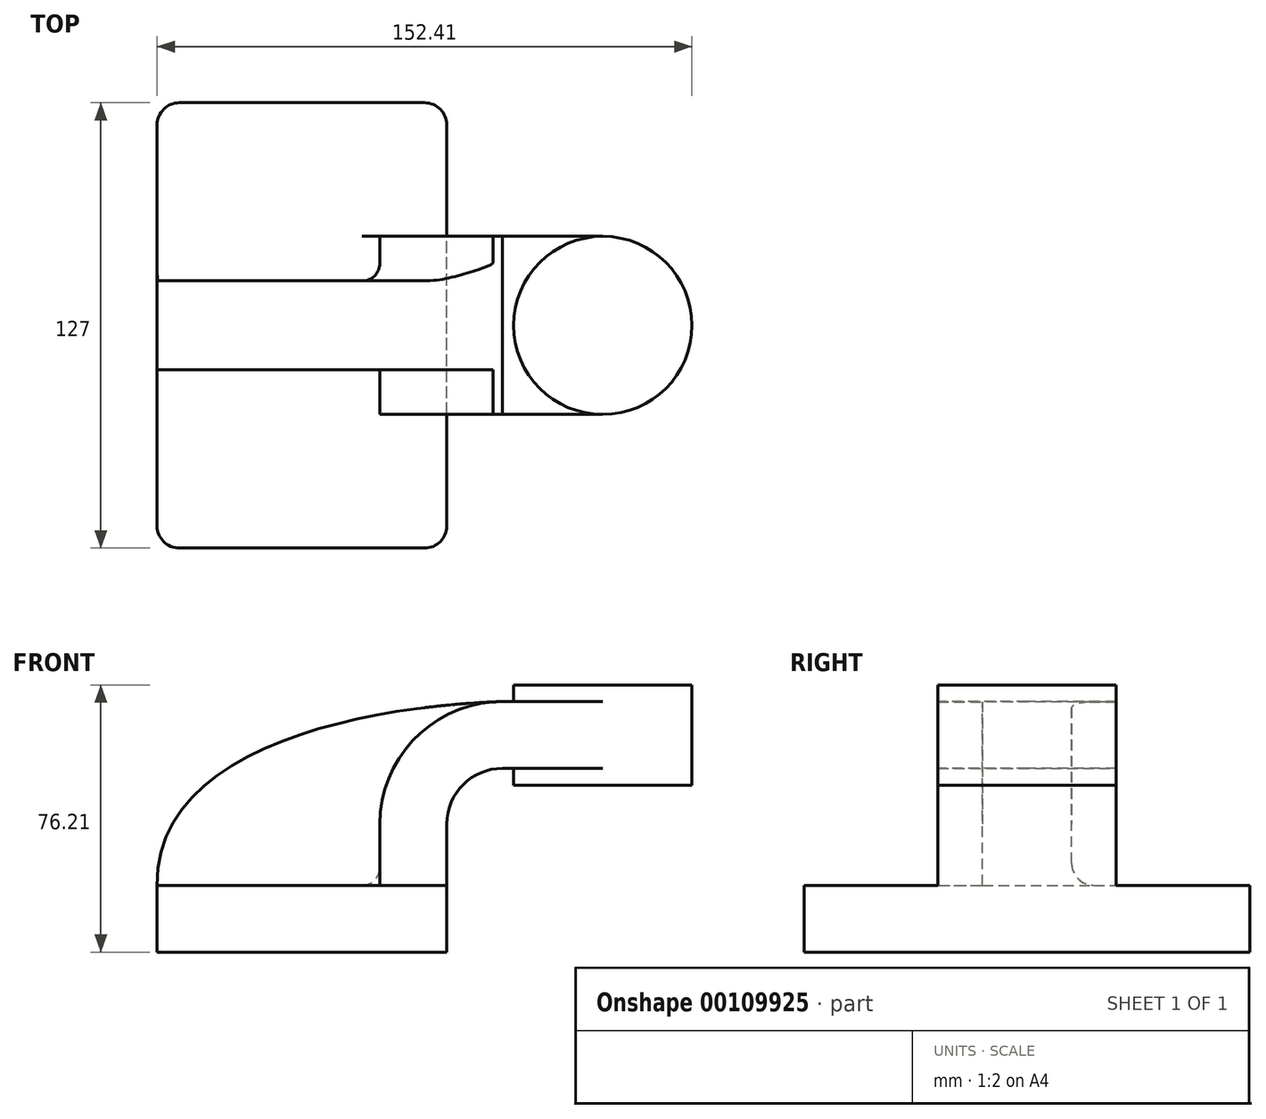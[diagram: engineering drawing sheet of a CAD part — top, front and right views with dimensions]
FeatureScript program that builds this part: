
annotation { "Feature Type Name" : "Feature", "Feature Type Description" : "" }
export const myFeature = defineFeature(function(context is Context, id is Id, definition is map)
    precondition{}
    {
        {
            var Q0;
            Q0=qCreatedBy(makeId("Front.planeOp"),FACE);
            var sketch = newSketch(context, id + "F0", { "sketchPlane" : qUnion([Q0])});
            skLineSegment(sketch, "E0.bottom", {"start": v(-41.27, -9.53) * mm, "end": v(41.28, -9.52) * mm});
            skLineSegment(sketch, "E0.top", {"start": v(-41.28, 9.52) * mm, "end": v(41.27, 9.53) * mm});
            skLineSegment(sketch, "E0.left", {"start": v(-41.27, -9.53) * mm, "end": v(-41.28, 9.52) * mm});
            skLineSegment(sketch, "E0.right", {"start": v(41.28, -9.52) * mm, "end": v(41.27, 9.53) * mm});
            skPoint(sketch, "E0.middle", {"position": v(0, 0) * mm});
            skLineSegment(sketch, "E1.bottom", {"start": v(111.13, 38.1) * mm, "end": v(60.33, 38.1) * mm});
            skLineSegment(sketch, "E1.top", {"start": v(111.13, 66.68) * mm, "end": v(60.33, 66.67) * mm});
            skLineSegment(sketch, "E1.left", {"start": v(111.13, 38.1) * mm, "end": v(111.13, 66.67) * mm});
            skLineSegment(sketch, "E1.right", {"start": v(60.33, 38.1) * mm, "end": v(60.33, 66.67) * mm});
            skPoint(sketch, "E1.middle", {"position": v(85.73, 52.39) * mm});
            skLineSegment(sketch, "E2", {"start": v(41.27, 9.53) * mm, "end": v(41.27, 27) * mm});
            skArc(sketch, "E3", {"start": v(41.28, 27) * mm, "mid": v(45.92, 38.23) * mm, "end": v(57.15, 42.88) * mm});
            skLineSegment(sketch, "E4", {"start": v(57.15, 42.88) * mm, "end": v(85.73, 42.88) * mm});
            skLineSegment(sketch, "E5.0", {"start": v(57.15, 61.93) * mm, "end": v(85.73, 61.93) * mm});
            skArc(sketch, "E5.1", {"start": v(22.23, 27) * mm, "mid": v(32.45, 51.7) * mm, "end": v(57.15, 61.93) * mm});
            skLineSegment(sketch, "E5.2", {"start": v(22.22, 9.53) * mm, "end": v(22.22, 27) * mm});
            skLineSegment(sketch, "E6", {"start": v(85.73, 38.1) * mm, "end": v(85.73, 66.67) * mm});
            skFitSpline(sketch, "E7", {"points": [v(-41.28, 9.52) * mm, v(57.15, 61.93) * mm], "startDerivative": vector(-1.57, 118.9) * mm, "endDerivative": vector(117.7, 4) * mm});
            skSolve(sketch);
        }
        {
            var Q0;
            Q0=makeQuery(id+"F0.imprint","IMPRINT",FACE,{"disambiguationData":[TD([[makeQuery(id+"F0.imprint","IMPRINT",EDGE,{"derivedFrom":sQuery(id+"F0.wireOp",EDGE,"E0.bottom")}),1.0]])]});
            extrude(context, id + "F1", {"entities" : qUnion([Q0]), "endBound" : BoundingType.SYMMETRIC, "depth" : 127 * mm});
        }
        {
            var Q0;
            {var subQ1=sQuery(id+"F0.wireOp",EDGE,"E2");Q0=makeQuery(id+"F0.imprint","IMPRINT",FACE,{"disambiguationData":[TD([[makeQuery(id+"F0.imprint","IMPRINT",EDGE,{"derivedFrom":subQ1}),1.0]])]});}
            extrude(context, id + "F2", {"entities" : qUnion([Q0]), "operationType" : NewBodyOperationType.ADD, "endBound" : BoundingType.SYMMETRIC, "depth" : 50.8 * mm});
        }
        {
            var Q0;
            {var subQ0=sQuery(id+"F0.wireOp",EDGE,"E4");var subQ1=sQuery(id+"F0.wireOp",EDGE,"E1.right");var subQ2=makeQuery(id+"F0.imprint","INTERSECT",VERTEX,{"derivedFrom":[subQ1,subQ0]});Q0=makeQuery(id+"F0.imprint","IMPRINT",FACE,{"disambiguationData":[TD([[makeQuery(id+"F0.imprint","IMPRINT",EDGE,{"disambiguationData":[TD([[subQ2,-1.0]])],"derivedFrom":subQ1}),-1.0]])]});}
            extrude(context, id + "F3", {"entities" : qUnion([Q0]), "operationType" : NewBodyOperationType.ADD, "endBound" : BoundingType.SYMMETRIC, "depth" : 50.8 * mm});
        }
        {
            var Q0;
            {var subQ3=sQuery(id+"F0.wireOp",EDGE,"E5.2");Q0=makeQuery(id+"F0.imprint","IMPRINT",FACE,{"disambiguationData":[TD([[makeQuery(id+"F0.imprint","IMPRINT",EDGE,{"derivedFrom":subQ3}),1.0]])]});}
            extrude(context, id + "F4", {"entities" : qUnion([Q0]), "operationType" : NewBodyOperationType.ADD, "endBound" : BoundingType.SYMMETRIC, "depth" : 25.4 * mm});
        }
        {
            var Q0;
            {var subQ0=sQuery(id+"F0.wireOp",EDGE,"E1.left");Q0=makeQuery(id+"F0.imprint","IMPRINT",FACE,{"disambiguationData":[TD([[makeQuery(id+"F0.imprint","IMPRINT",EDGE,{"derivedFrom":subQ0}),1.0]])]});}
            var Q1;
            Q1=sQuery(id+"F0.wireOp",EDGE,"E6");
            revolve(context, id + "F5", {"operationType" : NewBodyOperationType.ADD, "entities" : qUnion([Q0]), "axis" : qUnion([Q1]), "revolveType" : RevolveType.FULL});
        }
        {
            var Q0;
            Q0=makeQuery(id+"F1.opExtrude","CAP_EDGE",EDGE,{"disambiguationData":[OSD([sQuery(id+"F0.wireOp",EDGE,"E0.right")])],"isStart":false});
            var Q1;
            Q1=makeQuery(id+"F1.opExtrude","CAP_EDGE",EDGE,{"disambiguationData":[OSD([sQuery(id+"F0.wireOp",EDGE,"E0.left")])],"isStart":false});
            var Q2;
            Q2=makeQuery(id+"F1.opExtrude","CAP_EDGE",EDGE,{"disambiguationData":[OSD([sQuery(id+"F0.wireOp",EDGE,"E0.right")])],"isStart":true});
            var Q3;
            Q3=makeQuery(id+"F1.opExtrude","CAP_EDGE",EDGE,{"disambiguationData":[OSD([sQuery(id+"F0.wireOp",EDGE,"E0.left")])],"isStart":true});
            fillet(context, id + "F6", {"entities" : qUnion([Q0, Q1, Q2, Q3]), "radius" : 6.35 * mm, "tangentPropagation" : true, "allowEdgeOverflow" : false});
        }
        {
            var Q0;
            Q0=makeQuery(id+"F4.opExtrude","CAP_EDGE",EDGE,{"disambiguationData":[OSD([sQuery(id+"F0.wireOp",EDGE,"E0.top")])],"isStart":false});
            var Q1;
            Q1=makeQuery(id+"F2.opExtrude","CAP_EDGE",EDGE,{"disambiguationData":[OSD([sQuery(id+"F0.wireOp",EDGE,"E0.top")])],"isStart":false});
            var Q2;
            Q2=makeQuery(id+"F4.opExtrude","CAP_EDGE",EDGE,{"disambiguationData":[OSD([sQuery(id+"F0.wireOp",EDGE,"E0.top")])],"isStart":true});
            var Q3;
            Q3=makeQuery(id+"F2.opExtrude","CAP_EDGE",EDGE,{"disambiguationData":[OSD([sQuery(id+"F0.wireOp",EDGE,"E0.top")])],"isStart":true});
            var Q4;
            {var subQ0=sQuery(id+"F0.wireOp",EDGE,"E5.0");var subQ1=sQuery(id+"F0.wireOp",EDGE,"E4");var subQ2=sQuery(id+"F0.wireOp",EDGE,"E1.right");var subQ3=sQuery(id+"F0.wireOp",EDGE,"E5.2");var subQ6=sQuery(id+"F0.wireOp",EDGE,"E0.top");Q4=makeQuery(id+"F4.boolean.opBoolean","SPLIT",EDGE,{"disambiguationData":[TD([makeQuery(id+"F3.opExtrude","CAP_FACE",FACE,{"disambiguationData":[OSD([subQ2,subQ1,subQ0,sQuery(id+"F0.wireOp",EDGE,"E6")])],"isStart":true})])],"derivedFrom":makeQuery(id+"F2.opExtrude","SWEPT_EDGE",EDGE,{"disambiguationData":[OSD([subQ6,subQ3])]})});}
            var Q5;
            {var subQ0=sQuery(id+"F0.wireOp",EDGE,"E5.0");var subQ1=sQuery(id+"F0.wireOp",EDGE,"E4");var subQ2=sQuery(id+"F0.wireOp",EDGE,"E1.right");var subQ3=sQuery(id+"F0.wireOp",EDGE,"E5.2");var subQ6=sQuery(id+"F0.wireOp",EDGE,"E0.top");Q5=makeQuery(id+"F4.boolean.opBoolean","SPLIT",EDGE,{"disambiguationData":[TD([makeQuery(id+"F3.opExtrude","CAP_FACE",FACE,{"disambiguationData":[OSD([subQ2,subQ1,subQ0,sQuery(id+"F0.wireOp",EDGE,"E6")])],"isStart":false})])],"derivedFrom":makeQuery(id+"F2.opExtrude","SWEPT_EDGE",EDGE,{"disambiguationData":[OSD([subQ6,subQ3])]})});}
            fillet(context, id + "F7", {"entities" : qUnion([Q0, Q1, Q2, Q3, Q4, Q5]), "radius" : 6.35 * mm, "tangentPropagation" : true, "allowEdgeOverflow" : false});
        }
        {
            var Q0;
            Q0=makeQuery(id+"F4.opExtrude","CAP_EDGE",EDGE,{"disambiguationData":[OSD([sQuery(id+"F0.wireOp",EDGE,"E5.1")])],"isStart":false});
            var Q1;
            Q1=makeQuery(id+"F4.opExtrude","CAP_EDGE",EDGE,{"disambiguationData":[OSD([sQuery(id+"F0.wireOp",EDGE,"E5.2")])],"isStart":false});
            var Q2;
            {var subQ0=sQuery(id+"F0.wireOp",EDGE,"E5.0");var subQ1=sQuery(id+"F0.wireOp",EDGE,"E4");var subQ2=sQuery(id+"F0.wireOp",EDGE,"E1.right");var subQ3=sQuery(id+"F0.wireOp",EDGE,"E5.2");var subQ6=sQuery(id+"F0.wireOp",EDGE,"E0.top");Q2=makeQuery(id+"F7.opFillet","BLEND_EDGE",EDGE,{"blendedFrom":[makeQuery(id+"F4.opExtrude","CAP_EDGE",EDGE,{"disambiguationData":[OSD([subQ6])],"isStart":false}),makeQuery(id+"F4.boolean.opBoolean","SPLIT",EDGE,{"disambiguationData":[TD([makeQuery(id+"F3.opExtrude","CAP_FACE",FACE,{"disambiguationData":[OSD([subQ2,subQ1,subQ0,sQuery(id+"F0.wireOp",EDGE,"E6")])],"isStart":false})])],"derivedFrom":makeQuery(id+"F2.opExtrude","SWEPT_EDGE",EDGE,{"disambiguationData":[OSD([subQ6,subQ3])]})})],"blendedInto":[]});}
            var Q3;
            Q3=makeQuery(id+"F4.opExtrude","CAP_EDGE",EDGE,{"disambiguationData":[OSD([sQuery(id+"F0.wireOp",EDGE,"E5.2")])],"isStart":true});
            fillet(context, id + "F8", {"entities" : qUnion([Q0, Q1, Q2, Q3]), "radius" : 5.08 * mm, "tangentPropagation" : true, "allowEdgeOverflow" : false});
        }
    });
